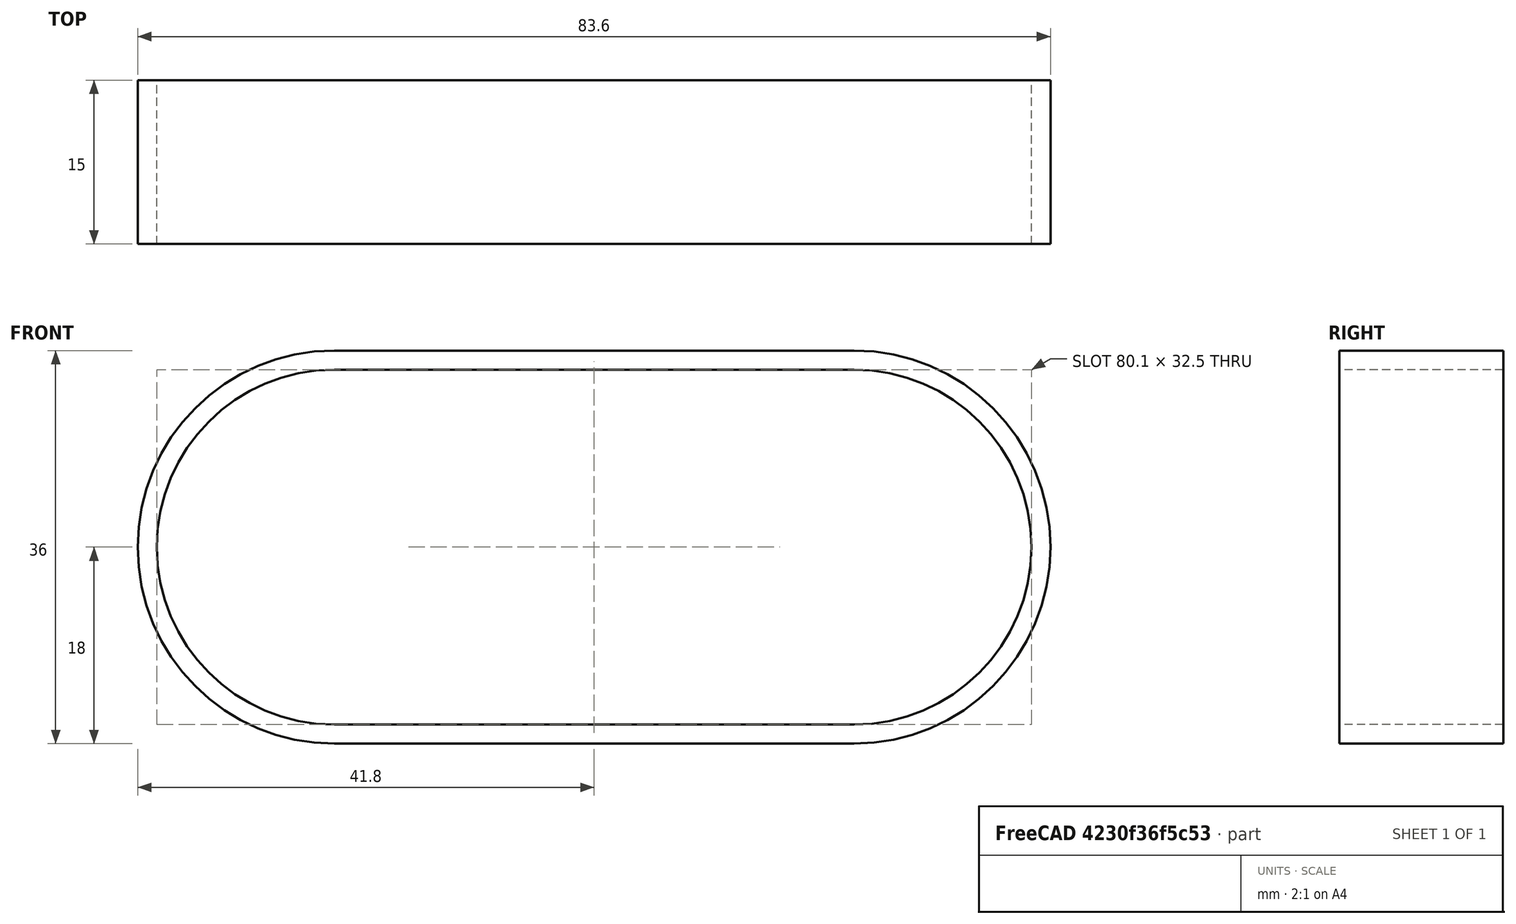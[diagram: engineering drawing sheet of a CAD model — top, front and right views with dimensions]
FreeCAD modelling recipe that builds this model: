
FCSTD DOCUMENT  (FreeCAD 0.21R33668 +7 (Git))
Label: GT2-220
License: All rights reserved
LicenseURL: https://en.wikipedia.org/wiki/All_rights_reserved
objects: Sketcher::SketchObject×1, PartDesign::Pad×1, PartDesign::Body×1
note: 4 computed .brp shape members not serialized (recipe doc carries the construction recipe); baked Part::Feature solids carry a one-line shape summary decoded from their .brp

FEATURE [Sketcher::SketchObject] Sketch
  FullyConstrained = true
  MapMode = 5
  Placement = pos=(0,0,0) rot=(1,0,0;1.5708rad)
  Support = -> [XZ_Plane]
  sketch-geometry (10):
    g0: ArcOfCircle CenterX=0 CenterY=0 CenterZ=0 NormalX=0 NormalY=0 NormalZ=1 AngleXU=0 Radius=18 StartAngle=1.5708 EndAngle=4.71239
    g1: ArcOfCircle CenterX=47.6 CenterY=0 CenterZ=0 NormalX=0 NormalY=0 NormalZ=1 AngleXU=0 Radius=18 StartAngle=4.71239 EndAngle=7.85398
    g2: LineSegment StartX=1.1e-15 StartY=18 StartZ=0 EndX=47.6 EndY=18 EndZ=0
    g3: LineSegment StartX=-3.3e-15 StartY=-18 StartZ=0 EndX=47.6 EndY=-18 EndZ=0
    g4: Circle CenterX=0 CenterY=0 CenterZ=0 NormalX=0 NormalY=0 NormalZ=1 AngleXU=0 Radius=17
    g5: GeomPoint X=0 Y=17 Z=0
    g6: ArcOfCircle CenterX=0 CenterY=0 CenterZ=0 NormalX=0 NormalY=0 NormalZ=1 AngleXU=0 Radius=16.25 StartAngle=1.5708 EndAngle=4.71239
    g7: ArcOfCircle CenterX=47.6 CenterY=0 CenterZ=0 NormalX=0 NormalY=0 NormalZ=1 AngleXU=0 Radius=16.25 StartAngle=4.71239 EndAngle=7.85398
    g8: LineSegment StartX=1e-15 StartY=16.25 StartZ=0 EndX=47.6 EndY=16.25 EndZ=0
    g9: LineSegment StartX=-3e-15 StartY=-16.25 StartZ=0 EndX=47.6 EndY=-16.25 EndZ=0
  constraints (22):
    c: Coincident(g0,g-1)
    c: PointOnObject(g0,g-2)
    c: PointOnObject(g1,g-1)
    c: Coincident(g4,g0)
    c: PointOnObject(g5,g4)
    c: PointOnObject(g5,g-2)
    c: DistanceY(g5,g0) = 1
    c: DistanceX(g0,g1) = 47.6
    c: DistanceX(g0,g1) = 47.6
    c: Tangent(g2,g1) = 1.5708
    c: Tangent(g3,g1) = -1.5708
    c: Tangent(g3,g0) = -1.5708
    c: Tangent(g2,g0) = 1.5708
    c: Diameter(g4) = 34
    c: Coincident(g6,g0)
    c: PointOnObject(g6,g-2)
    c: Coincident(g7,g1)
    c: Tangent(g9,g7) = -1.5708
    c: Tangent(g8,g7) = 1.5708
    c: Tangent(g8,g6) = 1.5708
    c: Tangent(g9,g6) = -1.5708
    c: DistanceY(g6,g5) = 0.75
FEATURE [PartDesign::Pad] Pad
  Direction = (0,-1,-2e-16)
  Length = 15
  Length2 = 10
  Midplane = true
  Placement = pos=(0,0,0) rot=(1,0,0;1.5708rad)
  Profile = -> Sketch
  ReferenceAxis = -> Sketch [N_Axis]
  Type = 0
FEATURE [PartDesign::Body] Body  label="GT2-220"
  Group = -> [Sketch,Pad]
  Origin = -> Origin
  Tip = -> Pad
